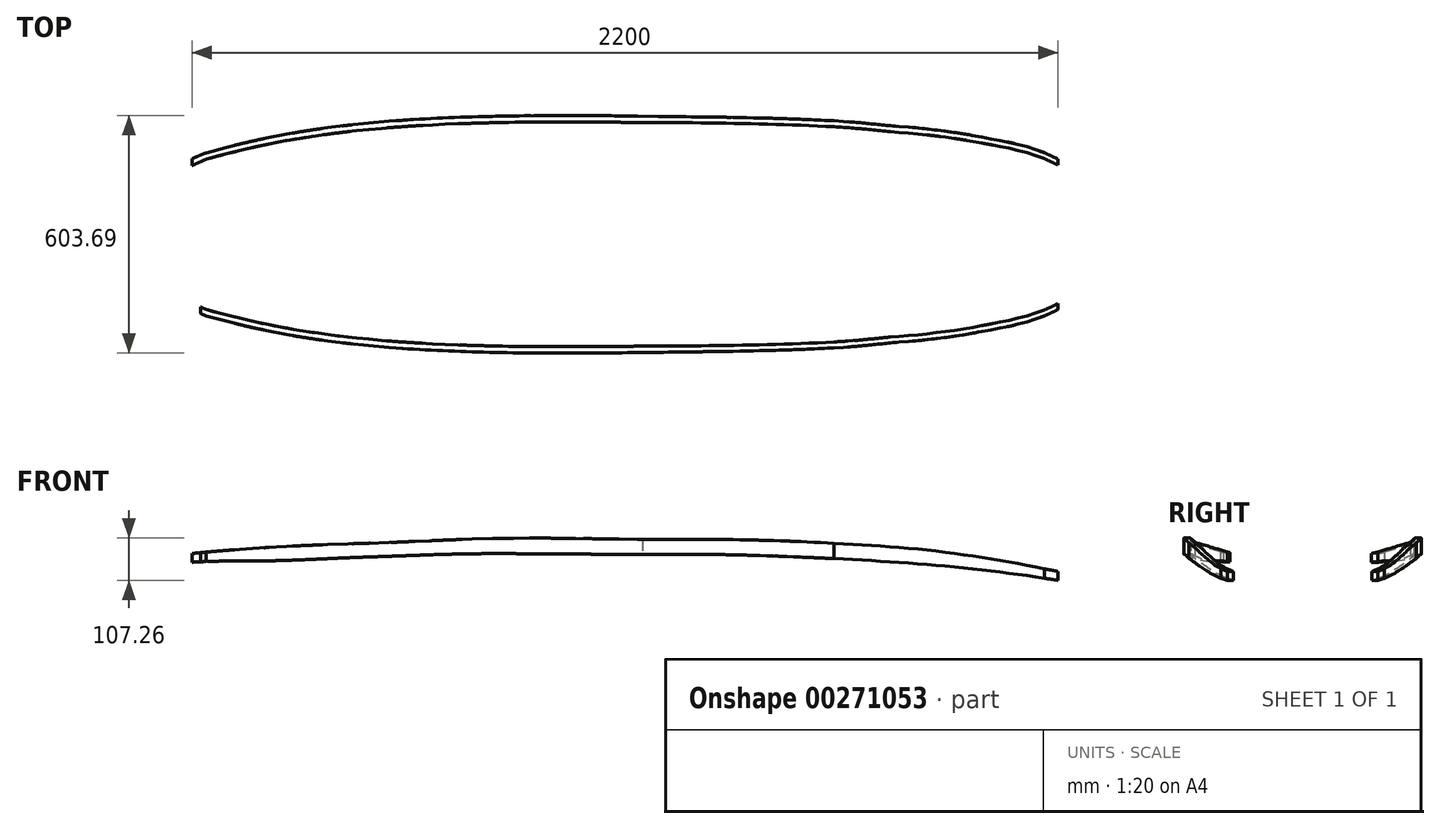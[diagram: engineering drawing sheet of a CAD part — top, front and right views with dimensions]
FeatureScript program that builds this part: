
annotation { "Feature Type Name" : "Feature", "Feature Type Description" : "" }
export const myFeature = defineFeature(function(context is Context, id is Id, definition is map)
    precondition{}
    {
        {
            var Q0;
            Q0=qCreatedBy(makeId("Top.planeOp"),FACE);
            var sketch = newSketch(context, id + "F0", { "sketchPlane" : qUnion([Q0])});
            skFitSpline(sketch, "E0", {"points": [v(4572.5, 526.74) * mm, v(4571.86, 509.8) * mm, v(4569.85, 493.74) * mm, v(4564.4, 472.79) * mm, v(4557.22, 453.27) * mm, v(4541.22, 425.42) * mm, v(4526.16, 406.9) * mm, v(4505.61, 386.63) * mm, v(4481, 366.94) * mm, v(4449.37, 348.93) * mm, v(4418.24, 334.47) * mm], "startDerivative": vector(-4.36, -212.72) * mm, "endDerivative": vector(-267.93, -120.02) * mm});
            skFitSpline(sketch, "E1", {"points": [v(4418.24, 334.47) * mm, v(4403.11, 329.32) * mm, v(4385.32, 323.04) * mm, v(4369.62, 318.15) * mm, v(4353.22, 314.32) * mm, v(4336.12, 309.43) * mm, v(4319.37, 306.64) * mm, v(4297.39, 302.1) * mm, v(4260.75, 295.12) * mm, v(4211.9, 286.4) * mm, v(4158.52, 278.73) * mm, v(4088.63, 270.86) * mm, v(4043.92, 267.35) * mm, v(3989.57, 262.1) * mm, v(3934.34, 256.83) * mm, v(3884.36, 253.32) * mm], "startDerivative": vector(-320.86, -107.7) * mm, "endDerivative": vector(-608.26, -38.86) * mm});
            skFitSpline(sketch, "E2", {"points": [v(3884.36, 253.32) * mm, v(3729.94, 247.06) * mm, v(3490.32, 242.88) * mm, v(3386.04, 242.88) * mm, v(3257.85, 245.78) * mm], "startDerivative": vector(-556.24, -26.96) * mm, "endDerivative": vector(-593.13, 15.55) * mm});
            skFitSpline(sketch, "E3", {"points": [v(3257.85, 245.78) * mm, v(3074.47, 254.38) * mm, v(2958.14, 264.13) * mm, v(2863.56, 272.83) * mm], "startDerivative": vector(-486.59, 18.91) * mm, "endDerivative": vector(-327.09, 29.83) * mm});
            skFitSpline(sketch, "E4", {"points": [v(2863.56, 272.83) * mm, v(2750.57, 287.15) * mm, v(2651.76, 303.05) * mm, v(2565.43, 317.82) * mm, v(2472.56, 338.8) * mm, v(2416.05, 352.43) * mm, v(2369.96, 365.65) * mm, v(2324.84, 380.04) * mm, v(2283.3, 396.14) * mm], "startDerivative": vector(-727.62, 85.49) * mm, "endDerivative": vector(-416.83, 168.93) * mm});
            skFitSpline(sketch, "E5", {"points": [v(2283.3, 396.14) * mm, v(2251.62, 406.53) * mm, v(2224.1, 419.5) * mm, v(2200.21, 429.9) * mm, v(2184.11, 438.2) * mm, v(2174.82, 444.95) * mm], "startDerivative": vector(-134.96, 39.06) * mm, "endDerivative": vector(-61.49, 47.96) * mm});
            skLineSegment(sketch, "E6", {"start": v(2174.82, 526.74) * mm, "end": v(2174.82, 444.95) * mm});
            skFitSpline(sketch, "E7.MirrorCS", {"points": [v(4418.24, 719.02) * mm, v(4403.11, 724.16) * mm, v(4385.32, 730.44) * mm, v(4369.62, 735.33) * mm, v(4353.22, 739.17) * mm, v(4336.12, 744.05) * mm, v(4319.37, 746.84) * mm, v(4297.39, 751.38) * mm, v(4260.75, 758.36) * mm, v(4211.9, 767.08) * mm, v(4158.52, 774.76) * mm, v(4088.63, 782.63) * mm, v(4043.92, 786.13) * mm, v(3989.57, 791.4) * mm, v(3934.34, 796.65) * mm, v(3884.36, 800.16) * mm], "startDerivative": vector(-320.86, 107.7) * mm, "endDerivative": vector(-608.26, 38.86) * mm});
            skFitSpline(sketch, "E8.MirrorCS", {"points": [v(4572.5, 526.74) * mm, v(4571.86, 543.67) * mm, v(4569.85, 559.74) * mm, v(4564.4, 580.7) * mm, v(4557.22, 600.2) * mm, v(4541.22, 628.06) * mm, v(4526.16, 646.6) * mm, v(4505.61, 666.85) * mm, v(4481, 686.54) * mm, v(4449.37, 704.55) * mm, v(4418.24, 719.02) * mm], "startDerivative": vector(-4.36, 212.72) * mm, "endDerivative": vector(-267.93, 120.02) * mm});
            skFitSpline(sketch, "E9.MirrorCS", {"points": [v(3884.36, 800.16) * mm, v(3729.94, 806.43) * mm, v(3490.32, 810.6) * mm, v(3386.04, 810.6) * mm, v(3257.85, 807.7) * mm], "startDerivative": vector(-556.24, 26.96) * mm, "endDerivative": vector(-593.13, -15.55) * mm});
            skFitSpline(sketch, "E10.MirrorCS", {"points": [v(3257.85, 807.7) * mm, v(3074.47, 799.1) * mm, v(2958.14, 789.35) * mm, v(2863.56, 780.65) * mm], "startDerivative": vector(-486.59, -18.91) * mm, "endDerivative": vector(-327.09, -29.83) * mm});
            skFitSpline(sketch, "E11.MirrorCS", {"points": [v(2863.56, 780.65) * mm, v(2750.57, 766.33) * mm, v(2651.76, 750.43) * mm, v(2565.43, 735.66) * mm, v(2472.56, 714.68) * mm, v(2416.05, 701.06) * mm, v(2369.96, 687.83) * mm, v(2324.84, 673.44) * mm, v(2283.3, 657.34) * mm], "startDerivative": vector(-727.62, -85.49) * mm, "endDerivative": vector(-416.83, -168.93) * mm});
            skFitSpline(sketch, "E12.MirrorCS", {"points": [v(2283.3, 657.34) * mm, v(2251.62, 646.95) * mm, v(2224.1, 633.97) * mm, v(2200.21, 623.59) * mm, v(2184.11, 615.28) * mm, v(2174.82, 608.53) * mm], "startDerivative": vector(-134.96, -39.06) * mm, "endDerivative": vector(-61.49, -47.96) * mm});
            skLineSegment(sketch, "E13.MirrorCS", {"start": v(2174.82, 526.74) * mm, "end": v(2174.82, 608.53) * mm});
            skFitSpline(sketch, "E14", {"points": [v(1525.82, -748.84) * mm, v(1510.7, -754) * mm, v(1492.9, -760.27) * mm, v(1477.2, -765.16) * mm, v(1460.8, -769) * mm, v(1443.7, -773.88) * mm, v(1426.96, -776.67) * mm, v(1404.98, -781.2) * mm, v(1368.34, -788.19) * mm, v(1319.5, -796.9) * mm, v(1266.1, -804.59) * mm, v(1196.22, -812.45) * mm, v(1151.5, -815.96) * mm, v(1097.15, -821.22) * mm, v(1041.92, -826.48) * mm, v(991.95, -829.99) * mm], "startDerivative": vector(-320.86, -107.7) * mm, "endDerivative": vector(-608.26, -38.86) * mm});
            skFitSpline(sketch, "E15", {"points": [v(991.95, -829.99) * mm, v(837.52, -836.25) * mm, v(597.9, -840.43) * mm, v(493.62, -840.43) * mm, v(365.44, -837.53) * mm], "startDerivative": vector(-556.24, -26.96) * mm, "endDerivative": vector(-593.13, 15.55) * mm});
            skFitSpline(sketch, "E16", {"points": [v(365.44, -837.53) * mm, v(182.06, -828.93) * mm, v(65.73, -819.18) * mm, v(-28.85, -810.48) * mm], "startDerivative": vector(-486.59, 18.91) * mm, "endDerivative": vector(-327.09, 29.83) * mm});
            skFitSpline(sketch, "E17", {"points": [v(-28.85, -810.48) * mm, v(-141.84, -796.16) * mm, v(-240.66, -780.26) * mm, v(-326.98, -765.5) * mm, v(-419.85, -744.51) * mm, v(-476.36, -730.89) * mm, v(-522.46, -717.66) * mm, v(-567.57, -703.27) * mm, v(-609.12, -687.17) * mm], "startDerivative": vector(-727.62, 85.49) * mm, "endDerivative": vector(-416.83, 168.93) * mm});
            skFitSpline(sketch, "E18", {"points": [v(-609.12, -687.17) * mm, v(-640.8, -676.78) * mm, v(-668.32, -663.8) * mm, v(-692.2, -653.42) * mm, v(-708.3, -645.1) * mm, v(-717.59, -638.36) * mm], "startDerivative": vector(-134.96, 39.06) * mm, "endDerivative": vector(-61.49, 47.96) * mm});
            skLineSegment(sketch, "E19", {"start": v(-717.59, -556.57) * mm, "end": v(-717.59, -638.36) * mm});
            skFitSpline(sketch, "E20.MirrorCS", {"points": [v(1525.82, -364.3) * mm, v(1510.7, -359.15) * mm, v(1492.9, -352.87) * mm, v(1477.2, -347.98) * mm, v(1460.8, -344.14) * mm, v(1443.7, -339.26) * mm, v(1426.96, -336.47) * mm, v(1404.98, -331.93) * mm, v(1368.34, -324.95) * mm, v(1319.5, -316.23) * mm, v(1266.1, -308.55) * mm, v(1196.22, -300.69) * mm, v(1151.5, -297.18) * mm, v(1097.15, -291.92) * mm, v(1041.92, -286.66) * mm, v(991.95, -283.15) * mm], "startDerivative": vector(-320.86, 107.7) * mm, "endDerivative": vector(-608.26, 38.86) * mm});
            skFitSpline(sketch, "E21.MirrorCS", {"points": [v(991.95, -283.15) * mm, v(837.52, -276.89) * mm, v(597.9, -272.7) * mm, v(493.62, -272.7) * mm, v(365.44, -275.6) * mm], "startDerivative": vector(-556.24, 26.96) * mm, "endDerivative": vector(-593.13, -15.55) * mm});
            skFitSpline(sketch, "E22.MirrorCS", {"points": [v(365.44, -275.6) * mm, v(182.06, -284.2) * mm, v(65.73, -293.96) * mm, v(-28.85, -302.66) * mm], "startDerivative": vector(-486.59, -18.91) * mm, "endDerivative": vector(-327.09, -29.83) * mm});
            skFitSpline(sketch, "E23.MirrorCS", {"points": [v(-28.85, -302.66) * mm, v(-141.84, -316.98) * mm, v(-240.66, -332.88) * mm, v(-326.98, -347.65) * mm, v(-419.85, -368.63) * mm, v(-476.36, -382.25) * mm, v(-522.46, -395.48) * mm, v(-567.57, -409.87) * mm, v(-609.12, -425.97) * mm], "startDerivative": vector(-727.62, -85.49) * mm, "endDerivative": vector(-416.83, -168.93) * mm});
            skFitSpline(sketch, "E24.MirrorCS", {"points": [v(-609.12, -425.97) * mm, v(-640.8, -436.36) * mm, v(-668.32, -449.34) * mm, v(-692.2, -459.72) * mm, v(-708.3, -468.03) * mm, v(-717.59, -474.78) * mm], "startDerivative": vector(-134.96, -39.06) * mm, "endDerivative": vector(-61.49, -47.96) * mm});
            skLineSegment(sketch, "E25.MirrorCS", {"start": v(-717.59, -556.57) * mm, "end": v(-717.59, -474.78) * mm});
            skFitSpline(sketch, "E26.MirrorCS", {"points": [v(1525.82, -349.2) * mm, v(1510.7, -344.05) * mm, v(1492.9, -337.77) * mm, v(1477.2, -332.88) * mm, v(1460.8, -329.05) * mm, v(1443.7, -324.16) * mm, v(1426.96, -321.37) * mm, v(1404.98, -316.83) * mm, v(1368.34, -309.86) * mm, v(1319.5, -301.13) * mm, v(1266.1, -293.46) * mm, v(1196.22, -285.59) * mm, v(1151.5, -282.08) * mm, v(1097.15, -276.82) * mm, v(1041.92, -271.56) * mm, v(991.95, -268.05) * mm], "startDerivative": vector(-320.86, 107.7) * mm, "endDerivative": vector(-608.26, 38.86) * mm});
            skFitSpline(sketch, "E27.MirrorCS", {"points": [v(991.95, -268.05) * mm, v(837.52, -261.79) * mm, v(597.9, -257.61) * mm, v(493.62, -257.61) * mm, v(365.44, -260.5) * mm], "startDerivative": vector(-556.24, 26.96) * mm, "endDerivative": vector(-593.13, -15.55) * mm});
            skFitSpline(sketch, "E28.MirrorCS", {"points": [v(365.44, -260.5) * mm, v(182.06, -269.1) * mm, v(65.73, -278.86) * mm, v(-28.85, -287.56) * mm], "startDerivative": vector(-486.59, -18.91) * mm, "endDerivative": vector(-327.09, -29.83) * mm});
            skFitSpline(sketch, "E29.MirrorCS", {"points": [v(-28.85, -287.56) * mm, v(-141.84, -301.88) * mm, v(-240.66, -317.78) * mm, v(-326.98, -332.55) * mm, v(-419.85, -353.53) * mm, v(-476.36, -367.16) * mm, v(-522.46, -380.38) * mm, v(-567.57, -394.78) * mm, v(-609.12, -410.87) * mm], "startDerivative": vector(-727.62, -85.49) * mm, "endDerivative": vector(-416.83, -168.93) * mm});
            skFitSpline(sketch, "E30.MirrorCS", {"points": [v(-609.12, -410.87) * mm, v(-640.8, -421.26) * mm, v(-668.32, -434.24) * mm, v(-692.2, -444.63) * mm, v(-708.3, -452.94) * mm, v(-717.59, -459.69) * mm], "startDerivative": vector(-134.96, -39.06) * mm, "endDerivative": vector(-61.49, -47.96) * mm});
            skLineSegment(sketch, "E31.MirrorCS", {"start": v(-717.59, -541.47) * mm, "end": v(-717.59, -459.69) * mm});
            skLineSegment(sketch, "E32", {"start": v(-717.59, -556.57) * mm, "end": v(1680.08, -556.57) * mm});
            skLineSegment(sketch, "E33.MirrorCS", {"start": v(-717.59, -571.67) * mm, "end": v(-717.59, -653.45) * mm});
            skFitSpline(sketch, "E34.MirrorCS", {"points": [v(-609.12, -702.27) * mm, v(-640.8, -691.88) * mm, v(-668.32, -678.9) * mm, v(-692.2, -668.51) * mm, v(-708.3, -660.2) * mm, v(-717.59, -653.45) * mm], "startDerivative": vector(-134.96, 39.06) * mm, "endDerivative": vector(-61.49, 47.96) * mm});
            skFitSpline(sketch, "E35.MirrorCS", {"points": [v(-28.85, -825.58) * mm, v(-141.84, -811.26) * mm, v(-240.66, -795.35) * mm, v(-326.98, -780.59) * mm, v(-419.85, -759.6) * mm, v(-476.36, -745.98) * mm, v(-522.46, -732.76) * mm, v(-567.57, -718.36) * mm, v(-609.12, -702.27) * mm], "startDerivative": vector(-727.62, 85.49) * mm, "endDerivative": vector(-416.83, 168.93) * mm});
            skFitSpline(sketch, "E36.MirrorCS", {"points": [v(365.44, -852.63) * mm, v(182.06, -844.03) * mm, v(65.73, -834.28) * mm, v(-28.85, -825.58) * mm], "startDerivative": vector(-486.59, 18.91) * mm, "endDerivative": vector(-327.09, 29.83) * mm});
            skFitSpline(sketch, "E37.MirrorCS", {"points": [v(991.95, -845.08) * mm, v(837.52, -851.35) * mm, v(597.9, -855.53) * mm, v(493.62, -855.53) * mm, v(365.44, -852.63) * mm], "startDerivative": vector(-556.24, -26.96) * mm, "endDerivative": vector(-593.13, 15.55) * mm});
            skFitSpline(sketch, "E38.MirrorCS", {"points": [v(1525.82, -763.94) * mm, v(1510.7, -769.09) * mm, v(1492.9, -775.37) * mm, v(1477.2, -780.25) * mm, v(1460.8, -784.1) * mm, v(1443.7, -788.98) * mm, v(1426.96, -791.77) * mm, v(1404.98, -796.3) * mm, v(1368.34, -803.28) * mm, v(1319.5, -812) * mm, v(1266.1, -819.68) * mm, v(1196.22, -827.55) * mm, v(1151.5, -831.06) * mm, v(1097.15, -836.32) * mm, v(1041.92, -841.58) * mm, v(991.95, -845.08) * mm], "startDerivative": vector(-320.86, -107.7) * mm, "endDerivative": vector(-608.26, -38.86) * mm});
            skLineSegment(sketch, "E39", {"start": v(1680.1, -541.47) * mm, "end": v(1680.08, -556.57) * mm});
            skLineSegment(sketch, "E40", {"start": v(1680.1, -571.67) * mm, "end": v(1680.08, -556.57) * mm});
            skLineSegment(sketch, "E41", {"start": v(1680.08, -556.57) * mm, "end": v(1580.08, -556.57) * mm});
            skLineSegment(sketch, "E42", {"start": v(1580.08, -331.62) * mm, "end": v(1580.08, -376.24) * mm});
            skLineSegment(sketch, "E43", {"start": v(1580.08, -376.24) * mm, "end": v(1580.08, -736.9) * mm});
            skFitSpline(sketch, "E44", {"points": [v(1680.08, -556.57) * mm, v(1679.45, -539.64) * mm, v(1677.44, -523.57) * mm, v(1671.98, -502.62) * mm, v(1664.8, -483.1) * mm, v(1648.8, -455.25) * mm, v(1633.75, -436.72) * mm, v(1613.2, -416.46) * mm, v(1588.6, -396.77) * mm, v(1556.96, -378.76) * mm, v(1525.82, -364.3) * mm], "startDerivative": vector(-4.36, 212.72) * mm, "endDerivative": vector(-267.93, 120.02) * mm});
            skFitSpline(sketch, "E45", {"points": [v(1680.08, -556.57) * mm, v(1679.45, -573.5) * mm, v(1677.44, -589.57) * mm, v(1671.98, -610.52) * mm, v(1664.8, -630.04) * mm, v(1648.8, -657.9) * mm, v(1633.75, -676.42) * mm, v(1613.2, -696.68) * mm, v(1588.6, -716.37) * mm, v(1556.96, -734.38) * mm, v(1525.82, -748.84) * mm], "startDerivative": vector(-4.36, -212.72) * mm, "endDerivative": vector(-267.93, -120.02) * mm});
            skLineSegment(sketch, "E46", {"start": v(1580.08, -736.9) * mm, "end": v(1580.08, -736.9) * mm});
            skLineSegment(sketch, "E47", {"start": v(1580.08, -376.24) * mm, "end": v(1580.08, -376.24) * mm});
            skLineSegment(sketch, "E48", {"start": v(1580.08, -736.9) * mm, "end": v(1580.08, -823.92) * mm});
            skFitSpline(sketch, "E49", {"points": [v(1680.1, -571.67) * mm, v(1679.45, -588.6) * mm, v(1677.44, -604.67) * mm, v(1671.98, -625.62) * mm, v(1664.8, -645.13) * mm, v(1648.8, -672.99) * mm, v(1633.75, -691.52) * mm, v(1613.2, -711.78) * mm, v(1588.6, -731.46) * mm, v(1556.96, -749.48) * mm, v(1525.82, -763.94) * mm], "startDerivative": vector(-4.36, -212.72) * mm, "endDerivative": vector(-267.93, -120.02) * mm});
            skFitSpline(sketch, "E50", {"points": [v(1680.1, -541.47) * mm, v(1679.45, -524.54) * mm, v(1677.44, -508.47) * mm, v(1671.98, -487.52) * mm, v(1664.8, -468) * mm, v(1648.8, -440.15) * mm, v(1633.75, -421.62) * mm, v(1613.2, -401.36) * mm, v(1588.6, -381.68) * mm, v(1556.96, -363.66) * mm, v(1525.82, -349.2) * mm], "startDerivative": vector(-4.36, 212.72) * mm, "endDerivative": vector(-267.93, 120.02) * mm});
            skLineSegment(sketch, "E51", {"start": v(-717.59, -597.46) * mm, "end": v(-717.59, -1180.66) * mm});
            skLineSegment(sketch, "E52", {"start": v(-717.59, -1180.66) * mm, "end": v(-717.59, 57.92) * mm});
            skFitSpline(sketch, "E53", {"points": [v(597.9, -855.53) * mm, v(87.83, -855.53) * mm, v(-471.72, -796.56) * mm, v(-717.59, -732.08) * mm, v(-717.59, -732.27) * mm], "startDerivative": vector(-1395.37, -20.82) * mm, "endDerivative": vector(12.82, -32.07) * mm});
            skLineSegment(sketch, "E54", {"start": v(-717.59, -732.08) * mm, "end": v(-717.59, -717.2) * mm});
            skFitSpline(sketch, "E55", {"points": [v(597.9, -839.23) * mm, v(87.83, -839.23) * mm, v(-471.72, -780.25) * mm, v(-717.59, -715.78) * mm, v(-717.59, -715.97) * mm], "startDerivative": vector(-1395.37, -20.82) * mm, "endDerivative": vector(12.82, -32.07) * mm});
            skFitSpline(sketch, "E56.MirrorCS", {"points": [v(597.9, -257.61) * mm, v(87.83, -257.61) * mm, v(-471.72, -316.58) * mm, v(-717.59, -381.06) * mm, v(-717.59, -380.87) * mm], "startDerivative": vector(-1395.37, 20.82) * mm, "endDerivative": vector(12.82, 32.07) * mm});
            skFitSpline(sketch, "E57.MirrorCS", {"points": [v(597.9, -273.91) * mm, v(87.83, -273.91) * mm, v(-471.72, -332.88) * mm, v(-717.59, -397.36) * mm, v(-717.59, -397.17) * mm], "startDerivative": vector(-1395.37, 20.82) * mm, "endDerivative": vector(12.82, 32.07) * mm});
            skLineSegment(sketch, "E58", {"start": v(-717.59, -556.57) * mm, "end": v(-617.59, -556.57) * mm});
            skLineSegment(sketch, "E59", {"start": v(-617.59, -556.57) * mm, "end": v(-617.59, -923.11) * mm});
            skLineSegment(sketch, "E60", {"start": v(-617.59, -923.11) * mm, "end": v(-617.59, -177.37) * mm});
            skFitSpline(sketch, "E61", {"points": [v(-603.64, -763.76) * mm, v(-672.16, -733.74) * mm, v(-700.75, -714.69) * mm, v(-717.59, -697.6) * mm, v(-717.59, -697.31) * mm], "startDerivative": vector(-177.67, 72.97) * mm, "endDerivative": vector(3.53, 7.25) * mm});
            skFitSpline(sketch, "E62", {"points": [v(-602.14, -747.87) * mm, v(-627.6, -736.54) * mm, v(-666, -717.2) * mm, v(-692.34, -699.83) * mm, v(-717.59, -677.7) * mm], "startDerivative": vector(-105.04, 43.98) * mm, "endDerivative": vector(-101.46, 93.52) * mm});
            skFitSpline(sketch, "E63.MirrorCS", {"points": [v(-603.64, -349.38) * mm, v(-672.16, -379.4) * mm, v(-700.75, -398.45) * mm, v(-717.59, -415.55) * mm, v(-717.59, -415.83) * mm], "startDerivative": vector(-177.67, -72.97) * mm, "endDerivative": vector(3.53, -7.25) * mm});
            skFitSpline(sketch, "E64.MirrorCS", {"points": [v(-602.14, -365.27) * mm, v(-627.6, -376.6) * mm, v(-666, -395.93) * mm, v(-692.34, -413.3) * mm, v(-717.59, -435.45) * mm], "startDerivative": vector(-105.04, -43.98) * mm, "endDerivative": vector(-101.46, -93.52) * mm});
            skSolve(sketch);
        }
        {
            var Q0;
            {var subQ5=sQuery(id+"F0.wireOp",EDGE,"E61");var subQ7=sQuery(id+"F0.wireOp",EDGE,"E52");var subQ8=makeQuery(id+"F0.imprint","INTERSECT",VERTEX,{"disambiguationData":[OD(0.0)],"derivedFrom":[subQ7,subQ5]});Q0=makeQuery(id+"F0.imprint","IMPRINT",FACE,{"disambiguationData":[TD([[makeQuery(id+"F0.imprint","IMPRINT",EDGE,{"disambiguationData":[TD([[subQ8,1.0]])],"derivedFrom":subQ7}),-1.0]])]});}
            var Q1;
            {var subQ0=sQuery(id+"F0.wireOp",EDGE,"E60");var subQ1=sQuery(id+"F0.wireOp",EDGE,"E55");var subQ2=makeQuery(id+"F0.imprint","INTERSECT",VERTEX,{"derivedFrom":[subQ1,subQ0]});Q1=makeQuery(id+"F0.imprint","IMPRINT",FACE,{"disambiguationData":[TD([[makeQuery(id+"F0.imprint","IMPRINT",EDGE,{"disambiguationData":[TD([[subQ2,-1.0]])],"derivedFrom":subQ1}),1.0]])]});}
            var Q2;
            {var subQ2=sQuery(id+"F0.wireOp",EDGE,"E36.MirrorCS");var subQ5=sQuery(id+"F0.wireOp",EDGE,"E37.MirrorCS");var subQ9=makeQuery(id+"F0.imprint","INTERSECT",VERTEX,{"derivedFrom":[subQ2,subQ5]});Q2=makeQuery(id+"F0.imprint","IMPRINT",FACE,{"disambiguationData":[TD([[makeQuery(id+"F0.imprint","IMPRINT",EDGE,{"disambiguationData":[TD([[subQ9,-1.0]])],"derivedFrom":subQ2}),1.0]])]});}
            var Q3;
            {var subQ5=sQuery(id+"F0.wireOp",EDGE,"E63.MirrorCS");var subQ6=sQuery(id+"F0.wireOp",EDGE,"E52");var subQ9=makeQuery(id+"F0.imprint","INTERSECT",VERTEX,{"disambiguationData":[OD(0.0)],"derivedFrom":[subQ6,subQ5]});Q3=makeQuery(id+"F0.imprint","IMPRINT",FACE,{"disambiguationData":[TD([[makeQuery(id+"F0.imprint","IMPRINT",EDGE,{"disambiguationData":[TD([[subQ9,1.0]])],"derivedFrom":subQ6}),-1.0]])]});}
            var Q4;
            {var subQ0=sQuery(id+"F0.wireOp",EDGE,"E60");var subQ1=sQuery(id+"F0.wireOp",EDGE,"E57.MirrorCS");var subQ2=makeQuery(id+"F0.imprint","INTERSECT",VERTEX,{"derivedFrom":[subQ1,subQ0]});Q4=makeQuery(id+"F0.imprint","IMPRINT",FACE,{"disambiguationData":[TD([[makeQuery(id+"F0.imprint","IMPRINT",EDGE,{"disambiguationData":[TD([[subQ2,-1.0]])],"derivedFrom":subQ1}),-1.0]])]});}
            var Q5;
            {var subQ2=sQuery(id+"F0.wireOp",EDGE,"E28.MirrorCS");var subQ5=sQuery(id+"F0.wireOp",EDGE,"E27.MirrorCS");var subQ9=makeQuery(id+"F0.imprint","INTERSECT",VERTEX,{"derivedFrom":[subQ5,subQ2]});Q5=makeQuery(id+"F0.imprint","IMPRINT",FACE,{"disambiguationData":[TD([[makeQuery(id+"F0.imprint","IMPRINT",EDGE,{"disambiguationData":[TD([[subQ9,1.0]])],"derivedFrom":subQ5}),-1.0]])]});}
            var Q6;
            {var subQ0=sQuery(id+"F0.wireOp",EDGE,"E64.MirrorCS");var subQ1=sQuery(id+"F0.wireOp",EDGE,"E57.MirrorCS");var subQ2=makeQuery(id+"F0.imprint","INTERSECT",VERTEX,{"derivedFrom":[subQ1,subQ0]});Q6=makeQuery(id+"F0.imprint","IMPRINT",FACE,{"disambiguationData":[TD([[makeQuery(id+"F0.imprint","IMPRINT",EDGE,{"disambiguationData":[TD([[subQ2,-1.0]])],"derivedFrom":subQ1}),1.0]])]});}
            var Q7;
            {var subQ0=sQuery(id+"F0.wireOp",EDGE,"E62");var subQ1=sQuery(id+"F0.wireOp",EDGE,"E55");var subQ2=makeQuery(id+"F0.imprint","INTERSECT",VERTEX,{"derivedFrom":[subQ1,subQ0]});Q7=makeQuery(id+"F0.imprint","IMPRINT",FACE,{"disambiguationData":[TD([[makeQuery(id+"F0.imprint","IMPRINT",EDGE,{"disambiguationData":[TD([[subQ2,-1.0]])],"derivedFrom":subQ1}),-1.0]])]});}
            var Q8;
            {var subQ9=sQuery(id+"F0.wireOp",EDGE,"E14");Q8=makeQuery(id+"F0.imprint","IMPRINT",FACE,{"disambiguationData":[TD([[makeQuery(id+"F0.imprint","IMPRINT",EDGE,{"derivedFrom":subQ9}),1.0]])]});}
            var Q9;
            {var subQ4=sQuery(id+"F0.wireOp",EDGE,"E20.MirrorCS");Q9=makeQuery(id+"F0.imprint","IMPRINT",FACE,{"disambiguationData":[TD([[makeQuery(id+"F0.imprint","IMPRINT",EDGE,{"derivedFrom":subQ4}),-1.0]])]});}
            extrude(context, id + "F1", {"entities" : qUnion([Q0, Q1, Q2, Q3, Q4, Q5, Q6, Q7, Q8, Q9]), "depth" : 200 * mm});
        }
        {
            var Q0;
            Q0=qCreatedBy(makeId("Front.planeOp"),FACE);
            var sketch = newSketch(context, id + "F2", { "sketchPlane" : qUnion([Q0])});
            skLineSegment(sketch, "E65", {"start": v(1583.63, 44.88) * mm, "end": v(1583.63, 202.23) * mm});
            skPoint(sketch, "E65.endSnap0", {"position": v(1583.63, 44.88) * mm});
            skLineSegment(sketch, "E66", {"start": v(1583.63, 202.23) * mm, "end": v(-742.83, 202.23) * mm});
            skLineSegment(sketch, "E67", {"start": v(-742.83, 202.23) * mm, "end": v(-742.83, 0) * mm});
            skLineSegment(sketch, "E68", {"start": v(-742.83, 0) * mm, "end": v(1583.63, 0) * mm});
            skLineSegment(sketch, "E69", {"start": v(1583.63, 0) * mm, "end": v(1583.63, 22.87) * mm});
            skLineSegment(sketch, "E70", {"start": v(1560.45, 45.67) * mm, "end": v(1560.45, 92.4) * mm});
            skLineSegment(sketch, "E71", {"start": v(-639.55, 90.7) * mm, "end": v(-639.55, 134.48) * mm});
            skFitSpline(sketch, "E72", {"points": [v(1560.45, 77.46) * mm, v(1461.22, 97.14) * mm, v(1260.45, 128.16) * mm, v(1060.45, 145.02) * mm, v(860.45, 155.22) * mm, v(660.45, 159.1) * mm, v(460.45, 159.74) * mm, v(260.45, 162.2) * mm, v(60.45, 159.37) * mm, v(-139.55, 151.16) * mm, v(-339.55, 144.14) * mm, v(-539.55, 132.04) * mm, v(-639.55, 123.3) * mm], "startDerivative": vector(-1442.06, 299.73) * mm, "endDerivative": vector(-1462.9, -137.8) * mm});
            skFitSpline(sketch, "E73", {"points": [v(-639.55, 100.98) * mm, v(-573.05, 103.68) * mm, v(-434.9, 104.79) * mm, v(-248.77, 112.16) * mm, v(-119.41, 116.82) * mm, v(60.45, 122.36) * mm, v(260.45, 122.2) * mm, v(460.45, 121.34) * mm, v(660.45, 121.07) * mm, v(860.45, 116.04) * mm, v(1060.45, 106.47) * mm, v(1261.33, 92.45) * mm, v(1460.98, 69.83) * mm, v(1560.45, 55) * mm], "startDerivative": vector(1256.43, 68.59) * mm, "endDerivative": vector(1504.97, -237.88) * mm});
            skLineSegment(sketch, "E74", {"start": v(1583.63, 22.87) * mm, "end": v(1583.63, 44.88) * mm});
            skSolve(sketch);
        }
        {
            var Q0;
            {var subQ3=sQuery(id+"F2.wireOp",EDGE,"cf876554-18dd-4214-b544-1d778cc49dfa");Q0=makeQuery(id+"F2.imprint","IMPRINT",FACE,{"disambiguationData":[TD([[makeQuery(id+"F2.imprint","IMPRINT",EDGE,{"derivedFrom":subQ3}),1.0]])]});}
            var Q1;
            Q1=makeQuery(id+"F2.imprint","IMPRINT",FACE,{"disambiguationData":[TD([[makeQuery(id+"F2.imprint","IMPRINT",EDGE,{"derivedFrom":sQuery(id+"F2.wireOp",EDGE,"E65")}),1.0]])]});
            extrude(context, id + "F3", {"entities" : qUnion([Q0, Q1]), "operationType" : NewBodyOperationType.REMOVE, "depth" : 1970 * mm});
        }
    });
